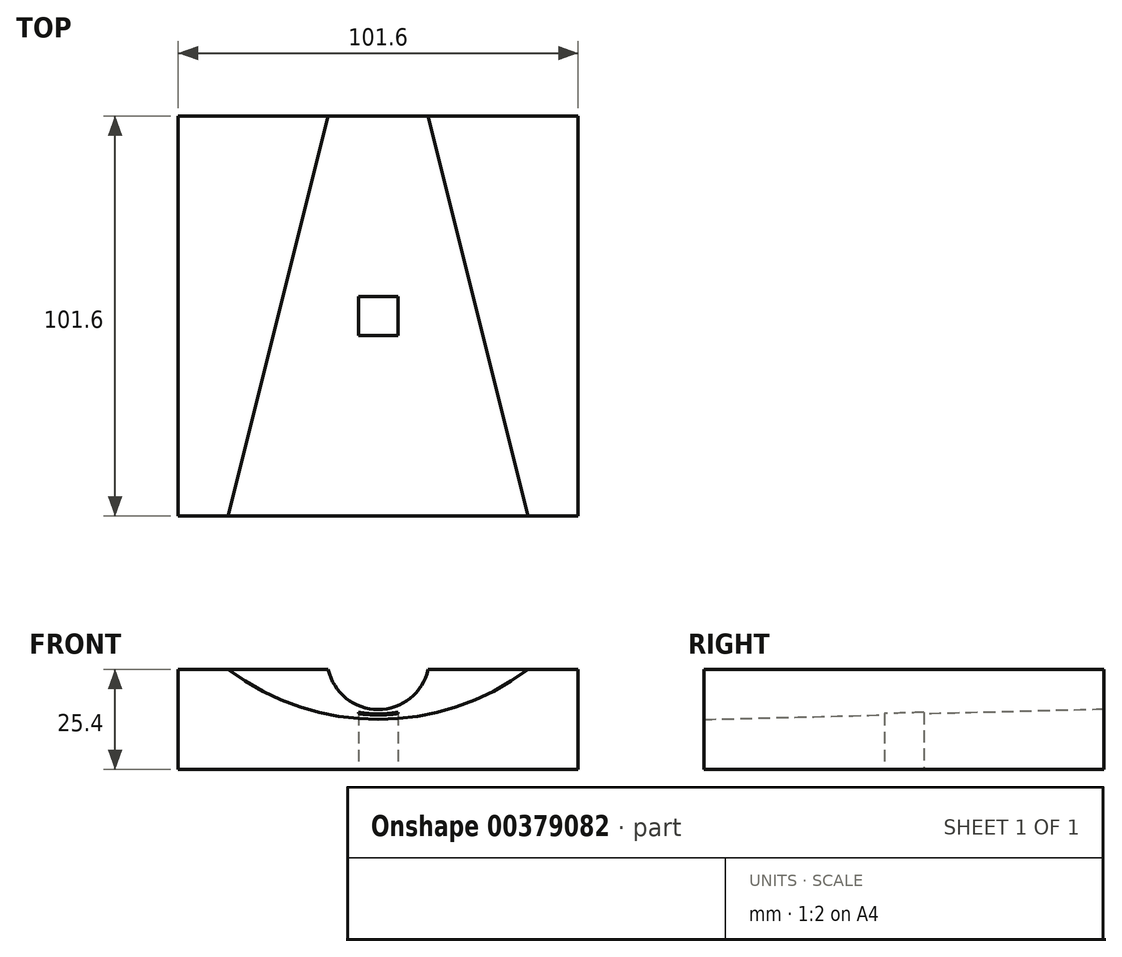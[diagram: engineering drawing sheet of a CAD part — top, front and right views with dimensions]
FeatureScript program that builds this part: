
annotation { "Feature Type Name" : "Feature", "Feature Type Description" : "" }
export const myFeature = defineFeature(function(context is Context, id is Id, definition is map)
    precondition{}
    {
        {
            var Q0;
            Q0=qCreatedBy(makeId("Front.planeOp"),FACE);
            var sketch = newSketch(context, id + "F0", { "sketchPlane" : qUnion([Q0])});
            skLineSegment(sketch, "E0.bottom", {"start": v(0, 0) * mm, "end": v(101.6, 0) * mm});
            skLineSegment(sketch, "E0.top", {"start": v(0, 25.4) * mm, "end": v(101.6, 25.4) * mm});
            skLineSegment(sketch, "E0.left", {"start": v(0, 0) * mm, "end": v(0, 25.4) * mm});
            skLineSegment(sketch, "E0.right", {"start": v(101.6, 0) * mm, "end": v(101.6, 25.4) * mm});
            skSolve(sketch);
        }
        {
            var Q0;
            Q0 = qSketchRegion(id + "F0", true);
            extrude(context, id + "F1", {"entities" : qUnion([Q0]), "oppositeDirection" : true, "depth" : 101.6 * mm});
        }
        {
            var Q0;
            Q0=makeQuery(id+"F1.opExtrude","CAP_FACE",FACE,{"disambiguationData":[OSD([sQuery(id+"F0.wireOp",EDGE,"E0.bottom"),sQuery(id+"F0.wireOp",EDGE,"E0.top"),sQuery(id+"F0.wireOp",EDGE,"E0.left"),sQuery(id+"F0.wireOp",EDGE,"E0.right")])],"isStart":true});
            var sketch = newSketch(context, id + "F2", { "sketchPlane" : qUnion([Q0])});
            skArc(sketch, "E1", {"start": v(12.7, 25.4) * mm, "mid": v(50.8, 12.7) * mm, "end": v(88.9, 25.4) * mm});
            skPoint(sketch, "E1.centerSnap0", {"position": v(50.8, 25.4) * mm});
            skLineSegment(sketch, "E2", {"start": v(101.6, 25.4) * mm, "end": v(0, 25.4) * mm, "construction": true});
            skSolve(sketch);
        }
        {
            var Q0;
            Q0=makeQuery(id+"F1.opExtrude","CAP_FACE",FACE,{"disambiguationData":[OSD([sQuery(id+"F0.wireOp",EDGE,"E0.bottom"),sQuery(id+"F0.wireOp",EDGE,"E0.top"),sQuery(id+"F0.wireOp",EDGE,"E0.left"),sQuery(id+"F0.wireOp",EDGE,"E0.right")])],"isStart":false});
            var sketch = newSketch(context, id + "F3", { "sketchPlane" : qUnion([Q0])});
            skArc(sketch, "E3", {"start": v(-63.5, 25.4) * mm, "mid": v(-50.8, 15.24) * mm, "end": v(-38.1, 25.4) * mm});
            skPoint(sketch, "E3.centerSnap0", {"position": v(-50.8, 25.4) * mm});
            skLineSegment(sketch, "E4", {"start": v(-101.6, 25.4) * mm, "end": v(0, 25.4) * mm, "construction": true});
            skSolve(sketch);
        }
        {
            var Q1;
            {var subQ0=sQuery(id+"F2.wireOp",EDGE,"E1");Q1=makeQuery(id+"F2.imprint","IMPRINT",FACE,{"disambiguationData":[TD([[makeQuery(id+"F2.imprint","IMPRINT",EDGE,{"derivedFrom":subQ0}),1.0]])]});}
            var Q2;
            {var subQ0=sQuery(id+"F3.wireOp",EDGE,"E3");Q2=makeQuery(id+"F3.imprint","IMPRINT",FACE,{"disambiguationData":[TD([[makeQuery(id+"F3.imprint","IMPRINT",EDGE,{"derivedFrom":subQ0}),1.0]])]});}
            loft(context, id + "F4", {"operationType" : NewBodyOperationType.REMOVE, "sheetProfilesArray" : [{ "sheetProfileEntities" : qUnion([Q1]) }, { "sheetProfileEntities" : qUnion([Q2]) }]});
        }
        {
            var Q0;
            Q0=makeQuery(id+"F1.opExtrude","SWEPT_FACE",FACE,{"disambiguationData":[OSD([sQuery(id+"F0.wireOp",EDGE,"E0.bottom")])]});
            var sketch = newSketch(context, id + "F5", { "sketchPlane" : qUnion([Q0])});
            skLineSegment(sketch, "E5.bottom", {"start": v(45.8, -55.8) * mm, "end": v(55.8, -55.8) * mm});
            skLineSegment(sketch, "E5.top", {"start": v(45.8, -45.8) * mm, "end": v(55.8, -45.8) * mm});
            skLineSegment(sketch, "E5.left", {"start": v(45.8, -55.8) * mm, "end": v(45.8, -45.8) * mm});
            skLineSegment(sketch, "E5.right", {"start": v(55.8, -55.8) * mm, "end": v(55.8, -45.8) * mm});
            skPoint(sketch, "E5.middle", {"position": v(50.8, -50.8) * mm});
            skPoint(sketch, "E5.middle.positionSnap0", {"position": v(50.8, -101.6) * mm});
            skPoint(sketch, "E5.middle.positionSnap1", {"position": v(0, -50.8) * mm});
            skPoint(sketch, "E5.centerSnap0", {"position": v(50.8, -101.6) * mm});
            skPoint(sketch, "E5.centerSnap1", {"position": v(0, -50.8) * mm});
            skSolve(sketch);
        }
        {
            var Q0;
            Q0 = qSketchRegion(id + "F5", true);
            var Q1;
            {var subQ0=sQuery(id+"F3.wireOp",EDGE,"E3");var subQ1=sQuery(id+"F0.wireOp",EDGE,"E0.top");var subQ2=makeQuery(id+"F1.opExtrude","CAP_EDGE",EDGE,{"disambiguationData":[OSD([subQ1])],"isStart":false});var subQ3=sQuery(id+"F2.wireOp",EDGE,"E1");var subQ4=makeQuery(id+"F1.opExtrude","CAP_EDGE",EDGE,{"disambiguationData":[OSD([subQ1])],"isStart":true});Q1=makeQuery(id+"F4.boolean.opBoolean","COPY",FACE,{"derivedFrom":makeQuery(id+"F4.opLoft","SWEPT_FACE",FACE,{"disambiguationData":[OSD([subQ1,subQ3,subQ0]),TDD([makeQuery(id+"F2.imprint","INTERSECT",VERTEX,{"disambiguationData":[OD(0.0)],"derivedFrom":[subQ4,subQ3]}),makeQuery(id+"F2.imprint","INTERSECT",VERTEX,{"disambiguationData":[OD(1.0)],"derivedFrom":[subQ4,subQ3]}),makeQuery(id+"F2.imprint","IMPRINT",EDGE,{"derivedFrom":subQ3}),makeQuery(id+"F3.imprint","INTERSECT",VERTEX,{"disambiguationData":[OD(0.0)],"derivedFrom":[subQ2,subQ0]}),makeQuery(id+"F3.imprint","INTERSECT",VERTEX,{"disambiguationData":[OD(1.0)],"derivedFrom":[subQ2,subQ0]}),makeQuery(id+"F3.imprint","IMPRINT",EDGE,{"derivedFrom":subQ0})])]})});}
            extrude(context, id + "F6", {"entities" : qUnion([Q0]), "operationType" : NewBodyOperationType.REMOVE, "endBound" : BoundingType.THROUGH_ALL, "oppositeDirection" : true, "endBoundEntityFace" : qUnion([Q1]), "depth" : 25.4 * mm});
        }
    });
